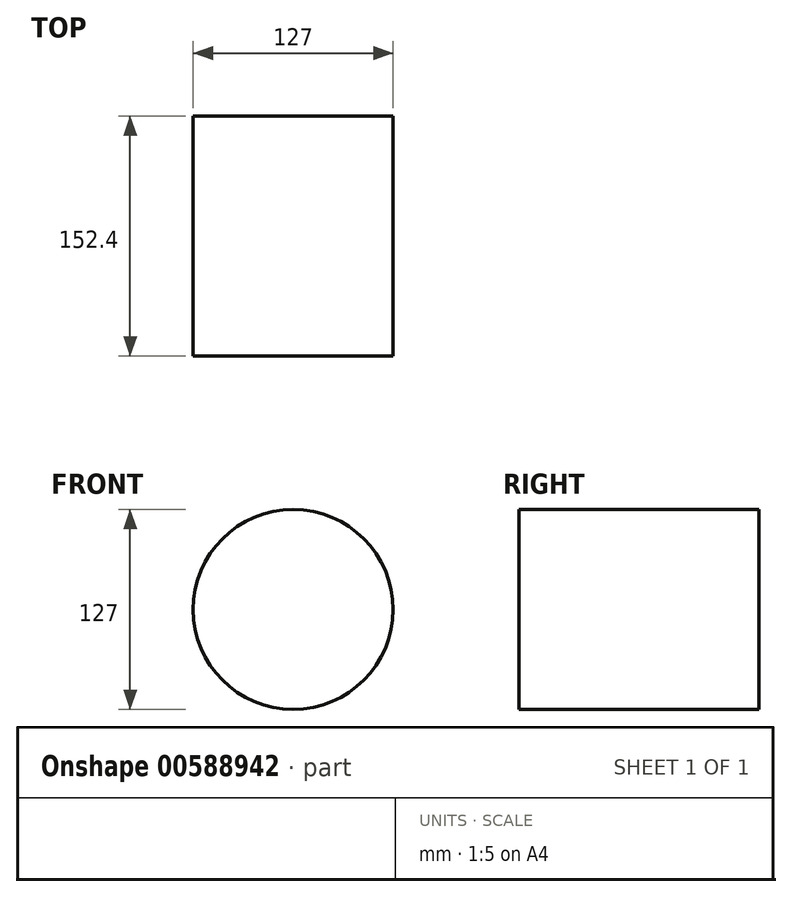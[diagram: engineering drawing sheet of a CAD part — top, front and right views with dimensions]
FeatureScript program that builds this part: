
annotation { "Feature Type Name" : "Feature", "Feature Type Description" : "" }
export const myFeature = defineFeature(function(context is Context, id is Id, definition is map)
    precondition{}
    {
        {
            var Q0;
            Q0=qCreatedBy(makeId("Front.planeOp"),FACE);
            var sketch = newSketch(context, id + "F0", { "sketchPlane" : qUnion([Q0])});
            skCircle(sketch, "E0", {"center": v(0, 0) * mm, "radius": 63.5 * mm});
            skSolve(sketch);
        }
        {
            var Q0;
            Q0 = qSketchRegion(id + "F0", true);
            extrude(context, id + "F1", {"entities" : qUnion([Q0]), "depth" : 152.4 * mm, "offsetDistance" : 25.4 * mm});
        }
    });
